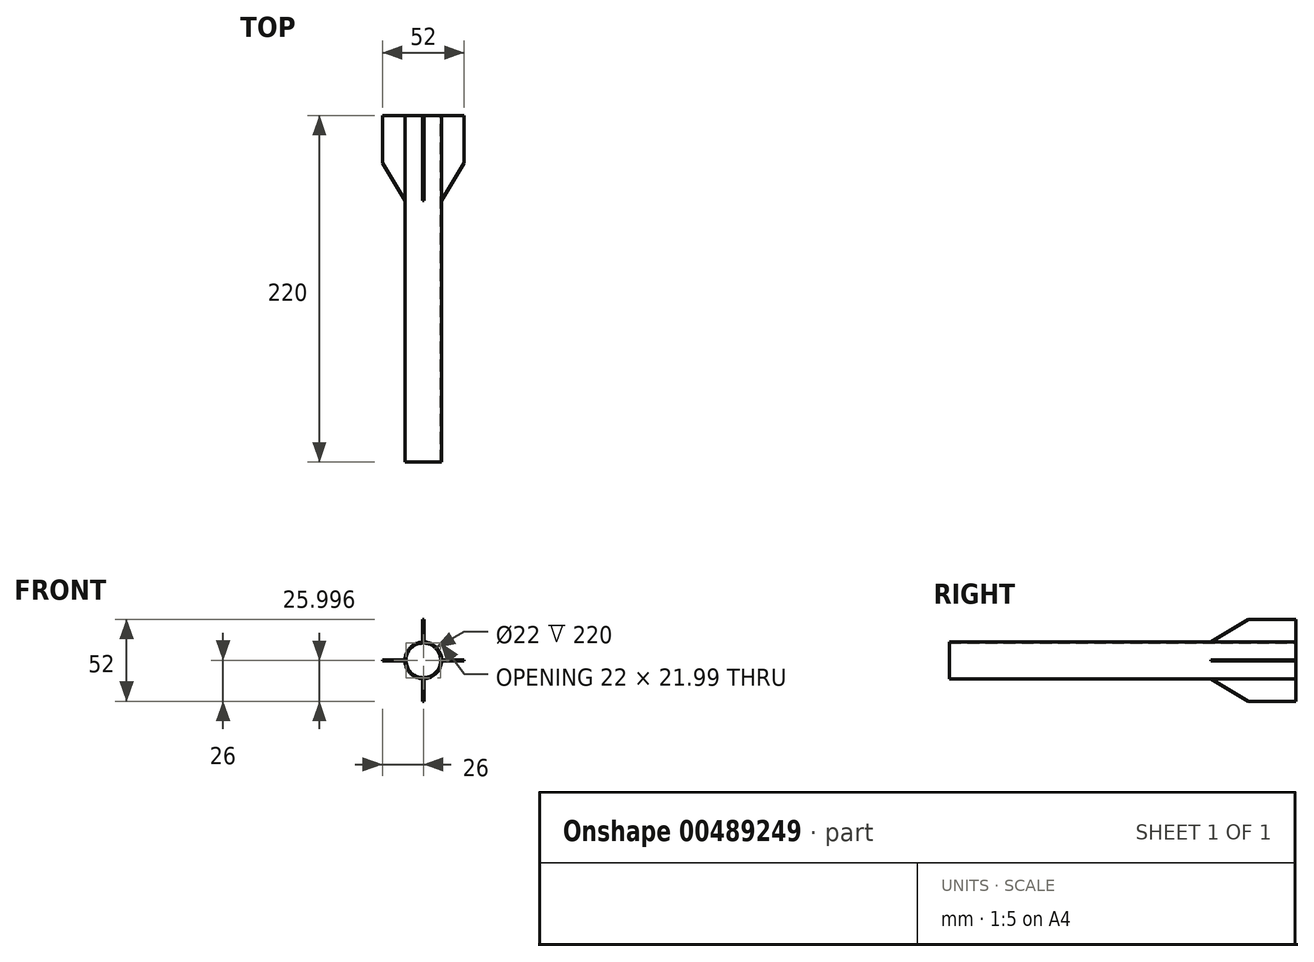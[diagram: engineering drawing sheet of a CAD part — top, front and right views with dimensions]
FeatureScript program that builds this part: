
annotation { "Feature Type Name" : "Feature", "Feature Type Description" : "" }
export const myFeature = defineFeature(function(context is Context, id is Id, definition is map)
    precondition{}
    {
        {
            var Q0;
            Q0=qCreatedBy(makeId("Front.planeOp"),FACE);
            var sketch = newSketch(context, id + "F0", { "sketchPlane" : qUnion([Q0])});
            skCircle(sketch, "E0", {"center": v(0, 0) * mm, "radius": 11 * mm});
            skCircle(sketch, "E1", {"center": v(0, 0) * mm, "radius": 11.65 * mm});
            skSolve(sketch);
        }
        {
            var Q0;
            Q0=makeQuery(id+"F0.imprint","IMPRINT",FACE,{"disambiguationData":[TD([[makeQuery(id+"F0.imprint","IMPRINT",EDGE,{"derivedFrom":sQuery(id+"F0.wireOp",EDGE,"E0")}),-1.0]])]});
            extrude(context, id + "F1", {"entities" : qUnion([Q0]), "depth" : 220 * mm});
        }
        {
            var Q0;
            Q0=qCreatedBy(makeId("Right.planeOp"),FACE);
            var sketch = newSketch(context, id + "F2", { "sketchPlane" : qUnion([Q0])});
            skLineSegment(sketch, "E2", {"start": v(0, 11) * mm, "end": v(-55, 11) * mm});
            skLineSegment(sketch, "E3", {"start": v(-55, 11) * mm, "end": v(-30.07, 26) * mm});
            skLineSegment(sketch, "E4", {"start": v(-30.07, 26) * mm, "end": v(0, 26) * mm});
            skLineSegment(sketch, "E5", {"start": v(0, 26) * mm, "end": v(0, 11) * mm});
            skSolve(sketch);
        }
        {
            var Q0;
            Q0=makeQuery(id+"F2.imprint","IMPRINT",FACE,{"disambiguationData":[TD([[makeQuery(id+"F2.imprint","IMPRINT",EDGE,{"derivedFrom":sQuery(id+"F2.wireOp",EDGE,"E2")}),-1.0]])]});
            extrude(context, id + "F3", {"entities" : qUnion([Q0]), "operationType" : NewBodyOperationType.ADD, "endBound" : BoundingType.SYMMETRIC, "depth" : 0.8 * mm});
        }
        {
            var Q0;
            Q0=makeQuery(id+"F1.opExtrude","SWEPT_BODY",BODY,{"disambiguationData":[OSD([sQuery(id+"F0.wireOp",EDGE,"E0"),sQuery(id+"F0.wireOp",EDGE,"E1")])]});
            var Q1;
            Q1=makeQuery(id+"F1.opExtrude","SWEPT_FACE",FACE,{"disambiguationData":[OSD([sQuery(id+"F0.wireOp",EDGE,"E1")])]});
            circularPattern(context, id + "F4", {"operationType" : NewBodyOperationType.ADD, "entities" : qUnion([Q0]), "axis" : qUnion([Q1]), "angle" : 360 * degree, "instanceCount" : 4, "equalSpace" : true});
        }
    });
